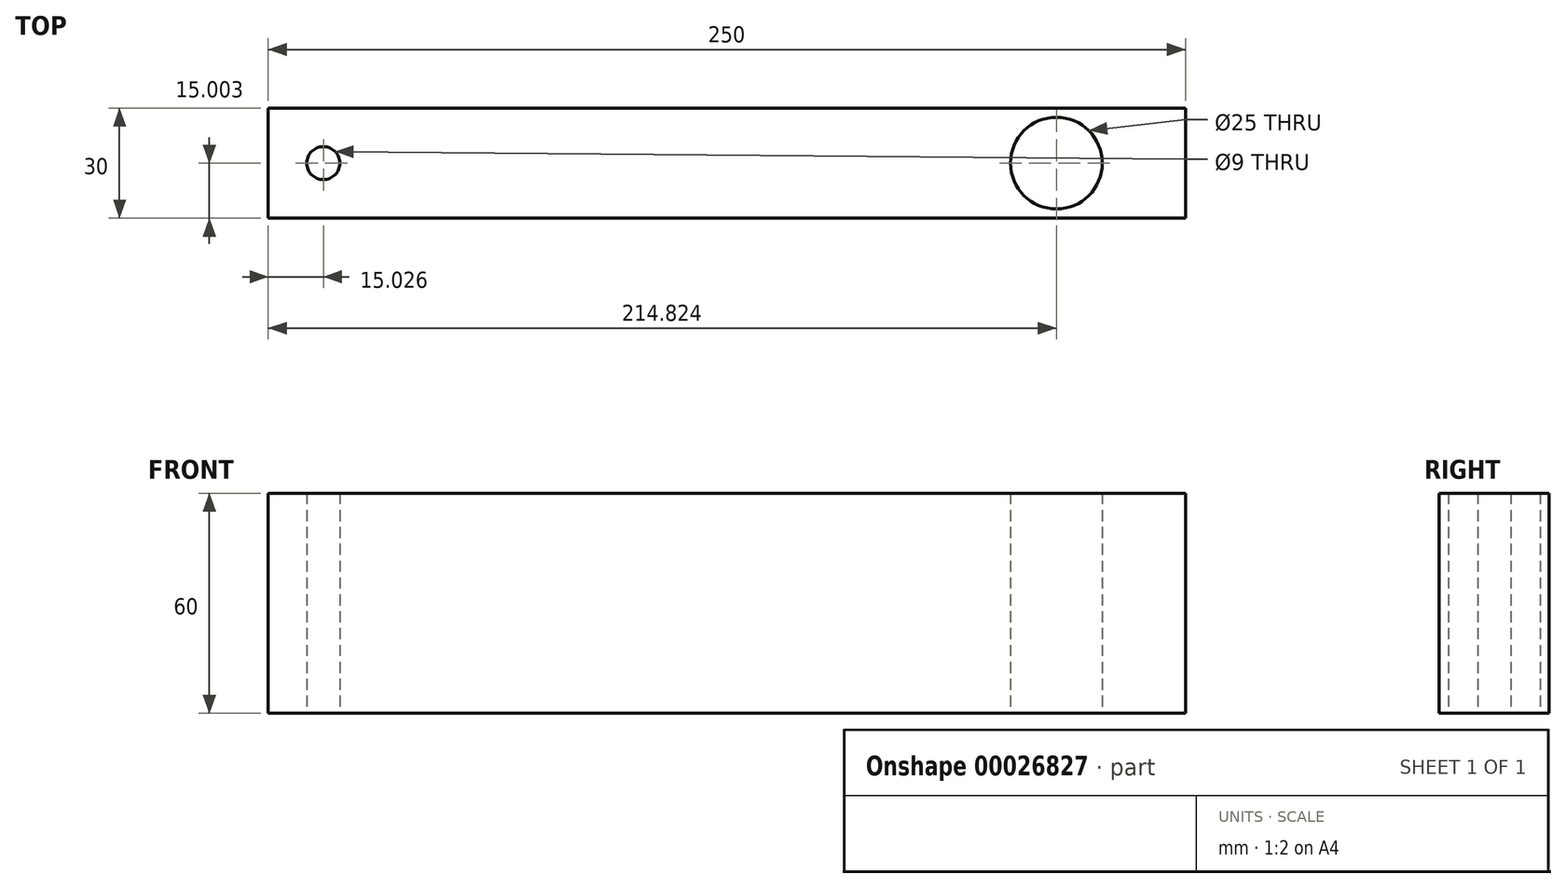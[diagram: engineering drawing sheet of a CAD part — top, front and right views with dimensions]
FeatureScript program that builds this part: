
annotation { "Feature Type Name" : "Feature", "Feature Type Description" : "" }
export const myFeature = defineFeature(function(context is Context, id is Id, definition is map)
    precondition{}
    {
        {
            var Q0;
            Q0=qCreatedBy(makeId("Top.planeOp"),FACE);
            var sketch = newSketch(context, id + "F0", { "sketchPlane" : qUnion([Q0])});
            skLineSegment(sketch, "E0.rect.bottom", {"start": v(-232.87, 2.38) * mm, "end": v(17.13, 2.38) * mm});
            skLineSegment(sketch, "E0.rect.top", {"start": v(-232.87, -27.62) * mm, "end": v(17.13, -27.62) * mm});
            skLineSegment(sketch, "E0.rect.left", {"start": v(-232.87, 2.38) * mm, "end": v(-232.87, -27.62) * mm});
            skLineSegment(sketch, "E0.rect.right", {"start": v(17.13, 2.38) * mm, "end": v(17.13, -27.62) * mm});
            skPoint(sketch, "E0.rect.middle", {"position": v(-107.87, -12.62) * mm});
            skLineSegment(sketch, "E1", {"start": v(17.13, -27.62) * mm, "end": v(17.13, -12.62) * mm});
            skLineSegment(sketch, "E2", {"start": v(17.13, -12.62) * mm, "end": v(-232.87, -12.62) * mm});
            skCircle(sketch, "E3", {"center": v(-18.05, -12.62) * mm, "radius": 12.5 * mm});
            skLineSegment(sketch, "E4", {"start": v(17.13, -12.62) * mm, "end": v(-17.87, -12.62) * mm});
            skCircle(sketch, "E5", {"center": v(-217.84, -12.62) * mm, "radius": 4.5 * mm});
            skSolve(sketch);
        }
        {
            var Q0;
            {var subQ7=sQuery(id+"F0.wireOp",EDGE,"E0.rect.top");Q0=makeQuery(id+"F0.imprint","IMPRINT",FACE,{"disambiguationData":[TD([[makeQuery(id+"F0.imprint","IMPRINT",EDGE,{"derivedFrom":subQ7}),1.0]])]});}
            var Q1;
            {var subQ7=sQuery(id+"F0.wireOp",EDGE,"E0.rect.bottom");Q1=makeQuery(id+"F0.imprint","IMPRINT",FACE,{"disambiguationData":[TD([[makeQuery(id+"F0.imprint","IMPRINT",EDGE,{"derivedFrom":subQ7}),-1.0]])]});}
            extrude(context, id + "F1", {"entities" : qUnion([Q0, Q1]), "depth" : 60 * mm});
        }
    });
